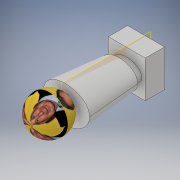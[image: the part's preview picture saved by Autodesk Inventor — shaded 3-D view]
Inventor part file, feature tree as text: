
AUTODESK INVENTOR PART (.ipt)
format: ipt  version: 2017 (Build 210142000, 142)  size: 261,120 bytes
history: native  units: in
note: dims shown in document units (in); Inventor stores cm internally (conversion verified against a paired STEP export)
features: sketch x5, extrude x4, projected_geometry x3, plane x1, revolve x1
ambient origin geometry x8: Origin, YZ Plane, XZ Plane, XY Plane, X Axis, Y Axis, Z Axis, Center Point
bodies: Solid1 (feature_tree)
feature tree (14):
  extrude  "Extrusion1"  Depth=0.575in
  extrude  "Extrusion2"  Depth=0.236in
  extrude  "Extrusion3"  Depth=0.115in TaperAngle=0.0deg
  plane  "Work Plane1"
  extrude  "Extrusion4"  Depth=0.84in
  revolve  "Revolution2"  Angle=90.0deg
  sketch  "Sketch1"  dims[d0=0.575in d1=0.575in]
  sketch  "Sketch2"  dims[d2=0.3in d3=0.0in d4=0.236in]
  sketch  "Sketch3"  dims[d5=0.155in d6=0.115in d7=0.0in]
  sketch  "Sketch4"  dims[d8=0.05in d9=0.84in d10=0.0344in]
  projected_geometry  "Projected Loop1"
  projected_geometry  "Projected Loop2"
  sketch  "Sketch6"  dims[d12=0.84in d13=0.0in d18=90.0deg]
  projected_geometry  "Projected Loop4"
